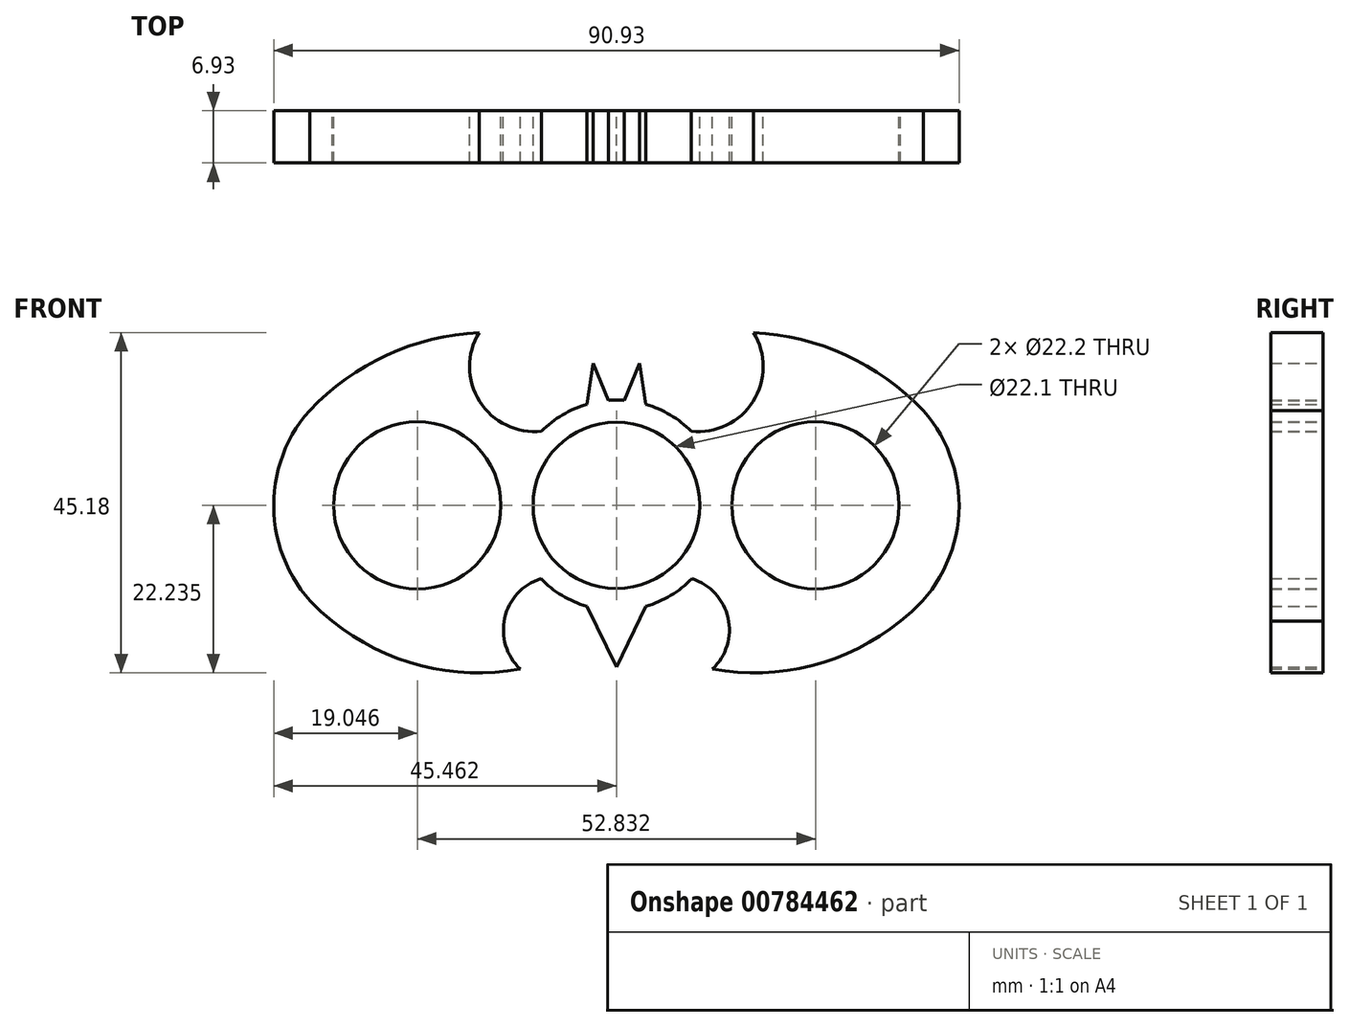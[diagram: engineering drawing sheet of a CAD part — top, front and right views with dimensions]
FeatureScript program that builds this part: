
annotation { "Feature Type Name" : "Feature", "Feature Type Description" : "" }
export const myFeature = defineFeature(function(context is Context, id is Id, definition is map)
    precondition{}
    {
        {
            var Q0;
            Q0=qCreatedBy(makeId("Front.planeOp"),FACE);
            var sketch = newSketch(context, id + "F0", { "sketchPlane" : qUnion([Q0])});
            skCircle(sketch, "E0", {"center": v(17.42, -21.9) * mm, "radius": 11.05 * mm});
            skCircle(sketch, "E1", {"center": v(17.42, -21.9) * mm, "radius": 13.97 * mm});
            skArc(sketch, "E2", {"start": v(55.1, -37.26) * mm, "mid": v(62.78, -23.94) * mm, "end": v(58.12, -9.3) * mm});
            skArc(sketch, "E3", {"start": v(-0.79, 1.05) * mm, "mid": v(-13.03, -1.96) * mm, "end": v(-23.28, -9.3) * mm});
            skArc(sketch, "E4", {"start": v(-0.79, 1.05) * mm, "mid": v(-0.73, -8.08) * mm, "end": v(7.5, -12.07) * mm});
            skArc(sketch, "E5.trimOffspring", {"start": v(-23.28, -9.3) * mm, "mid": v(-27.93, -23.94) * mm, "end": v(-20.26, -37.26) * mm});
            skArc(sketch, "E6.MirrorCS", {"start": v(35.63, 1.05) * mm, "mid": v(35.57, -8.08) * mm, "end": v(27.35, -12.07) * mm});
            skArc(sketch, "E7.MirrorCS", {"start": v(35.63, 1.05) * mm, "mid": v(47.87, -1.96) * mm, "end": v(58.12, -9.3) * mm});
            skArc(sketch, "E8", {"start": v(-20.26, -37.26) * mm, "mid": v(-8.5, -43.17) * mm, "end": v(4.66, -43.63) * mm});
            skArc(sketch, "E9", {"start": v(7.39, -31.62) * mm, "mid": v(2.6, -36.85) * mm, "end": v(4.66, -43.63) * mm});
            skArc(sketch, "E10.MirrorCS", {"start": v(27.45, -31.62) * mm, "mid": v(32.23, -36.85) * mm, "end": v(30.18, -43.63) * mm});
            skArc(sketch, "E11.MirrorCS", {"start": v(55.1, -37.26) * mm, "mid": v(43.34, -43.17) * mm, "end": v(30.18, -43.63) * mm});
            skPoint(sketch, "E12.end.orphan", {"position": v(19.76, -3.07) * mm});
            skPoint(sketch, "E13.orphan", {"position": v(21.34, -8.49) * mm});
            skPoint(sketch, "E14.end.orphan", {"position": v(16.38, -7.96) * mm});
            skPoint(sketch, "E15.end.orphan", {"position": v(15.2, -3.07) * mm});
            skPoint(sketch, "E16.MirrorCS.end.orphan", {"position": v(18.46, -7.96) * mm});
            skPoint(sketch, "E16.MirrorCS.start.orphan", {"position": v(19.65, -3.07) * mm});
            skPoint(sketch, "E17.end.orphan", {"position": v(12.61, -3.54) * mm});
            skPoint(sketch, "E18.MirrorCS.end.orphan", {"position": v(22.23, -3.54) * mm});
            skLineSegment(sketch, "E19", {"start": v(16.38, -7.96) * mm, "end": v(14.32, -3.06) * mm});
            skLineSegment(sketch, "E20", {"start": v(14.32, -3.06) * mm, "end": v(13.5, -8.49) * mm});
            skLineSegment(sketch, "E21.MirrorCS", {"start": v(18.46, -7.96) * mm, "end": v(20.52, -3.06) * mm});
            skLineSegment(sketch, "E22.MirrorCS", {"start": v(20.52, -3.06) * mm, "end": v(21.34, -8.49) * mm});
            skPoint(sketch, "E23.end.orphan", {"position": v(17.42, -43.35) * mm});
            skPoint(sketch, "E23.start.orphan", {"position": v(13.41, -35.28) * mm});
            skPoint(sketch, "E24.MirrorCS.start.orphan", {"position": v(21.43, -35.28) * mm});
            skPoint(sketch, "E25.MirrorCS.end.orphan", {"position": v(13.5, -35.3) * mm});
            skPoint(sketch, "E25.MirrorCS.start.orphan", {"position": v(14.32, -40.73) * mm});
            skLineSegment(sketch, "E26", {"start": v(13.5, -35.3) * mm, "end": v(17.42, -43.35) * mm});
            skLineSegment(sketch, "E27.MirrorCS", {"start": v(21.34, -35.3) * mm, "end": v(17.42, -43.35) * mm});
            skLineSegment(sketch, "E28", {"start": v(-9, -21.9) * mm, "end": v(-13.74, -21.9) * mm});
            skLineSegment(sketch, "E29", {"start": v(43.84, -21.9) * mm, "end": v(48.58, -21.9) * mm});
            skCircle(sketch, "E30", {"center": v(-9, -21.9) * mm, "radius": 11.1 * mm});
            skCircle(sketch, "E31", {"center": v(43.84, -21.9) * mm, "radius": 11.1 * mm});
            skSolve(sketch);
        }
        {
            var Q0;
            {var subQ0=sQuery(id+"F0.wireOp",EDGE,"E26");Q0=makeQuery(id+"F0.imprint","IMPRINT",FACE,{"disambiguationData":[TD([[makeQuery(id+"F0.imprint","IMPRINT",EDGE,{"derivedFrom":subQ0}),1.0]])]});}
            var Q1;
            {var subQ0=sQuery(id+"F0.wireOp",EDGE,"E21.MirrorCS");Q1=makeQuery(id+"F0.imprint","IMPRINT",FACE,{"disambiguationData":[TD([[makeQuery(id+"F0.imprint","IMPRINT",EDGE,{"derivedFrom":subQ0}),-1.0]])]});}
            var Q2;
            {var subQ0=sQuery(id+"F0.wireOp",EDGE,"E19");Q2=makeQuery(id+"F0.imprint","IMPRINT",FACE,{"disambiguationData":[TD([[makeQuery(id+"F0.imprint","IMPRINT",EDGE,{"derivedFrom":subQ0}),1.0]])]});}
            var Q3;
            Q3=makeQuery(id+"F0.imprint","IMPRINT",FACE,{"disambiguationData":[TD([[makeQuery(id+"F0.imprint","IMPRINT",EDGE,{"derivedFrom":sQuery(id+"F0.wireOp",EDGE,"E2")}),1.0]])]});
            var Q4;
            Q4=makeQuery(id+"F0.imprint","IMPRINT",FACE,{"disambiguationData":[TD([[makeQuery(id+"F0.imprint","IMPRINT",EDGE,{"derivedFrom":sQuery(id+"F0.wireOp",EDGE,"E0")}),-1.0]])]});
            var Q5;
            Q5=makeQuery(id+"F0.imprint","IMPRINT",FACE,{"disambiguationData":[TD([[makeQuery(id+"F0.imprint","IMPRINT",EDGE,{"derivedFrom":sQuery(id+"F0.wireOp",EDGE,"E3")}),1.0]])]});
            extrude(context, id + "F1", {"entities" : qUnion([Q0, Q1, Q2, Q3, Q4, Q5]), "depth" : 6.93 * mm, "offsetDistance" : 25.4 * mm});
        }
    });
